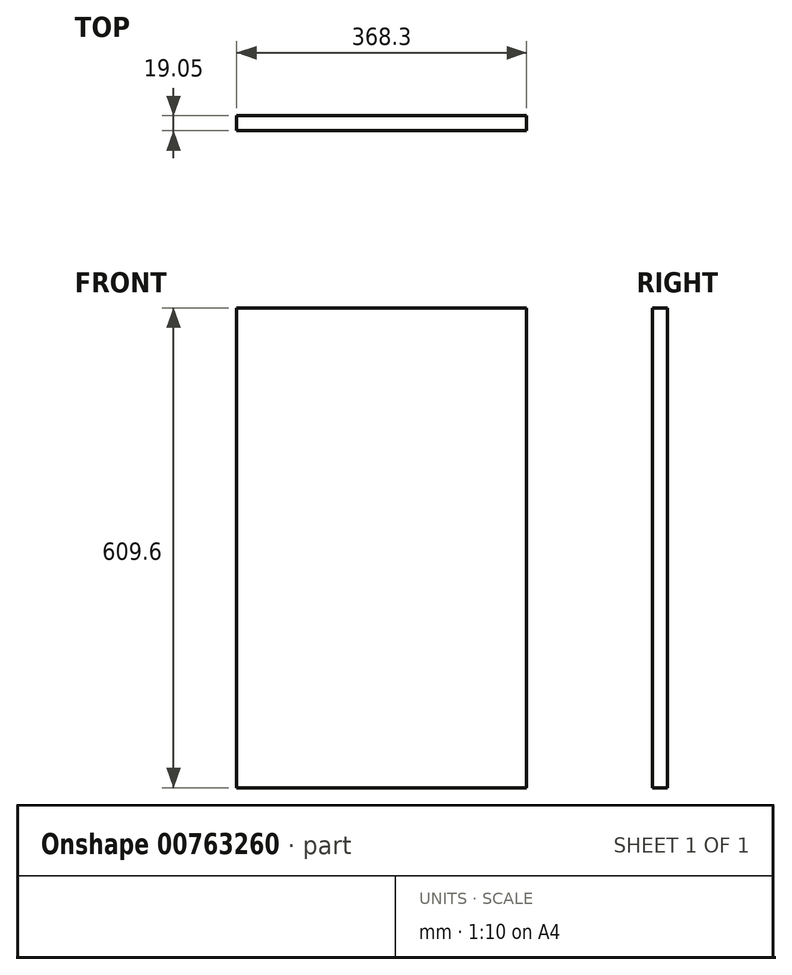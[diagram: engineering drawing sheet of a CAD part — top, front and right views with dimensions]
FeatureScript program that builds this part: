
annotation { "Feature Type Name" : "Feature", "Feature Type Description" : "" }
export const myFeature = defineFeature(function(context is Context, id is Id, definition is map)
    precondition{}
    {
        {
            var Q0;
            Q0=qCreatedBy(makeId("Front.planeOp"),FACE);
            var sketch = newSketch(context, id + "F0", { "sketchPlane" : qUnion([Q0])});
            skLineSegment(sketch, "E0.bottom", {"start": v(184.15, 304.8) * mm, "end": v(-184.15, 304.8) * mm});
            skLineSegment(sketch, "E0.top", {"start": v(184.15, -304.8) * mm, "end": v(-184.15, -304.8) * mm});
            skLineSegment(sketch, "E0.left", {"start": v(184.15, 304.8) * mm, "end": v(184.15, -304.8) * mm});
            skLineSegment(sketch, "E0.right", {"start": v(-184.15, 304.8) * mm, "end": v(-184.15, -304.8) * mm});
            skPoint(sketch, "E0.middle", {"position": v(0, 0) * mm});
            skSolve(sketch);
        }
        {
            var Q0;
            Q0 = qSketchRegion(id + "F0", true);
            extrude(context, id + "F1", {"entities" : qUnion([Q0]), "depth" : 19.05 * mm, "offsetDistance" : 25.4 * mm});
        }
    });
